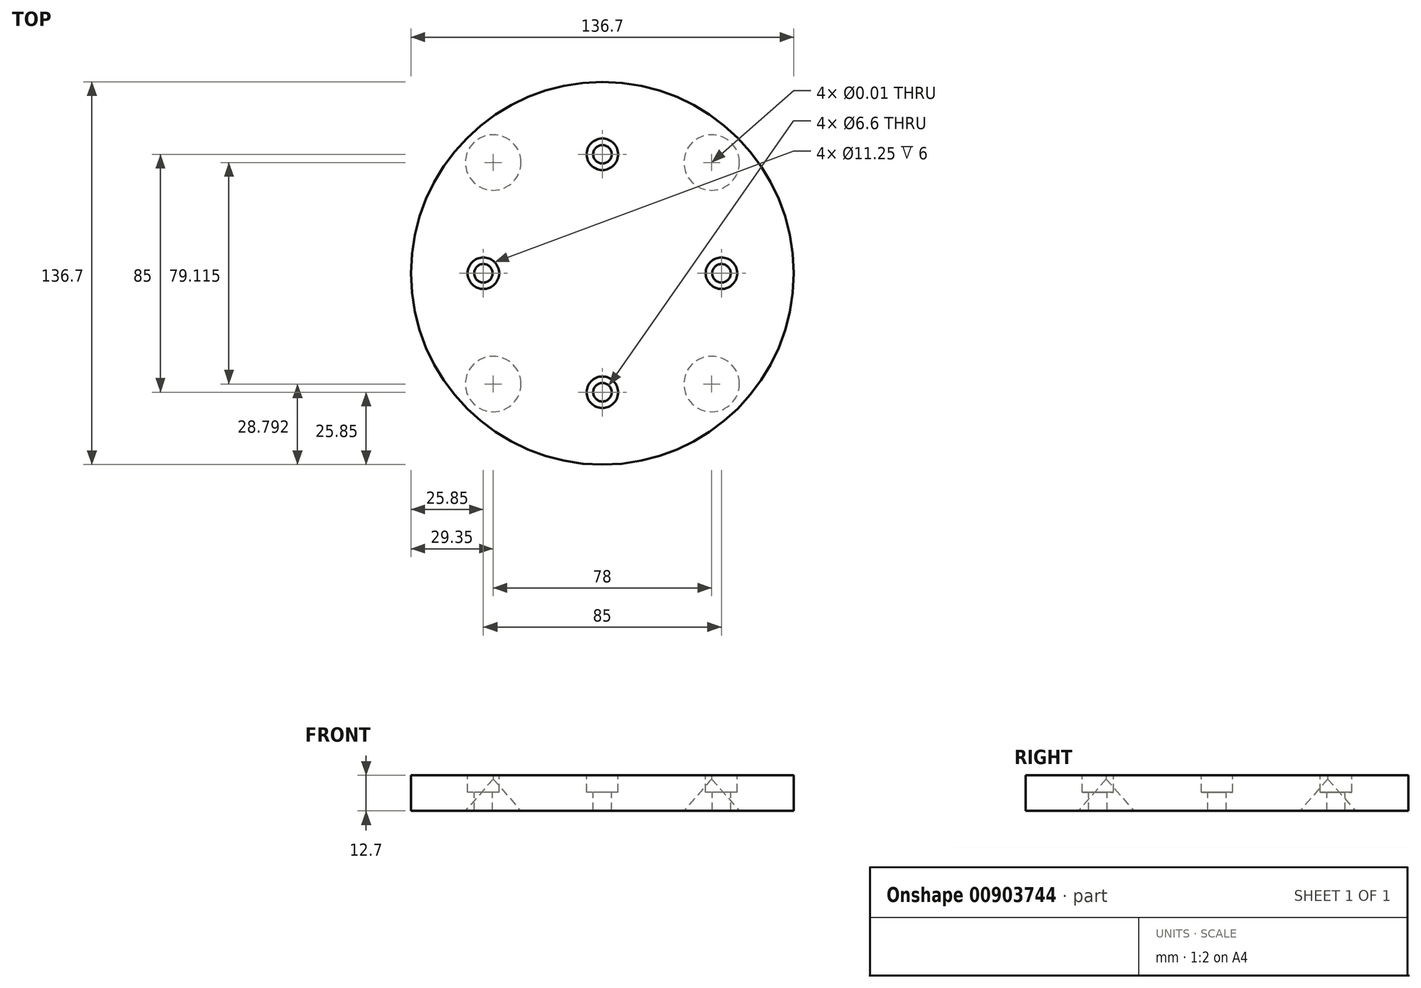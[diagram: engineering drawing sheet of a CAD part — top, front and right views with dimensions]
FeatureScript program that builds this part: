
annotation { "Feature Type Name" : "Feature", "Feature Type Description" : "" }
export const myFeature = defineFeature(function(context is Context, id is Id, definition is map)
    precondition{}
    {
        {
            var Q0;
            Q0=qCreatedBy(makeId("Top.planeOp"),FACE);
            cPlane(context, id + "F0", {"entities" : qUnion([Q0]), "cplaneType" : CPlaneType.OFFSET, "offset" : 12.7 * mm, "width" : 152.4 * mm, "height" : 152.4 * mm});
        }
        {
            var Q0;
            Q0=qCreatedBy(makeId("Top.planeOp"),FACE);
            var sketch = newSketch(context, id + "F1", { "sketchPlane" : qUnion([Q0])});
            skCircle(sketch, "E0", {"center": v(0, 0) * mm, "radius": 68.35 * mm});
            skSolve(sketch);
        }
        {
            var Q0;
            Q0 = qSketchRegion(id + "F1", true);
            extrude(context, id + "F2", {"entities" : qUnion([Q0]), "depth" : 12.7 * mm, "offsetDistance" : 25.4 * mm});
        }
        {
            var Q0;
            Q0=qCreatedBy(makeId("Top.planeOp"),FACE);
            var sketch = newSketch(context, id + "F3", { "sketchPlane" : qUnion([Q0])});
            skPoint(sketch, "E1", {"position": v(39, 39.56) * mm});
            skPoint(sketch, "E2", {"position": v(-39, 39.56) * mm});
            skPoint(sketch, "E3", {"position": v(-39, -39.56) * mm});
            skCircle(sketch, "E4", {"center": v(0, 0) * mm, "radius": 55.55 * mm});
            skPoint(sketch, "E5.MirrorP", {"position": v(39, -39.56) * mm});
            skSolve(sketch);
        }
        {
            var Q0;
            Q0=sQuery(id+"F3.wireOp",VERTEX,"E2");
            var Q1;
            Q1=sQuery(id+"F3.wireOp",VERTEX,"E1");
            var Q2;
            Q2=sQuery(id+"F3.wireOp",VERTEX,"f3bf48b2-0e91-47d8-8b82-7dac251cd858");
            var Q3;
            Q3=sQuery(id+"F3.wireOp",VERTEX,"E3");
            var Q4;
            Q4=sQuery(id+"F3.wireOp",VERTEX,"E5.MirrorP");
            var Q5;
            Q5=makeQuery(id+"F2.opExtrude","SWEPT_BODY",BODY,{"disambiguationData":[OSD([sQuery(id+"F1.wireOp",EDGE,"E0")])]});
            hole(context, id + "F4", {"style" : HoleStyle.C_SINK, "endStyle" : HoleEndStyle.THROUGH, "oppositeDirection" : true, "standardTappedOrClearance" : lookupTablePath({ "standard" : "ANSI", "size" : "3/8 (0.38)", "type" : "Drilled" }), "standardBlindInLast" : lookupTablePath({ "standard" : "ANSI", "size" : "3/8", "type" : "Drilled" }), "holeDiameter" : 3 / 203.2 * mm, "cSinkDiameter" : 19.84 * mm, "cSinkAngle" : 82 * degree, "majorDiameter" : 6.35 * mm, "isTappedThrough" : true, "tappedDepth" : 12.7 * mm, "tapClearance" : 3, "startFromSketch" : true, "locations" : qUnion([Q0, Q1, Q2, Q3, Q4]), "scope" : qUnion([Q5])});
        }
        {
            var Q0;
            Q0=qCreatedBy(id+"F0.planeOp",FACE);
            var sketch = newSketch(context, id + "F5", { "sketchPlane" : qUnion([Q0])});
            skPoint(sketch, "E6", {"position": v(0, 42.5) * mm});
            skPoint(sketch, "E7", {"position": v(42.5, 0) * mm});
            skPoint(sketch, "E8", {"position": v(-42.5, 0) * mm});
            skPoint(sketch, "E9", {"position": v(0, -42.5) * mm});
            skSolve(sketch);
        }
        {
            var Q0;
            Q0=sQuery(id+"F5.wireOp",VERTEX,"E6");
            var Q1;
            Q1=sQuery(id+"F5.wireOp",VERTEX,"E7");
            var Q2;
            Q2=sQuery(id+"F5.wireOp",VERTEX,"E9");
            var Q3;
            Q3=sQuery(id+"F5.wireOp",VERTEX,"E8");
            var Q4;
            Q4=makeQuery(id+"F2.opExtrude","SWEPT_BODY",BODY,{"disambiguationData":[OSD([sQuery(id+"F1.wireOp",EDGE,"E0")])]});
            hole(context, id + "F6", {"style" : HoleStyle.C_BORE, "endStyle" : HoleEndStyle.THROUGH, "standardTappedOrClearance" : lookupTablePath({ "fit" : "Normal", "standard" : "ISO", "size" : "M6", "type" : "Clearance" }), "standardBlindInLast" : lookupTablePath({ "fit" : "Normal", "standard" : "ISO", "size" : "M6", "type" : "Clearance" }), "holeDiameter" : 6.6 * mm, "cBoreDiameter" : 11.25 * mm, "cBoreDepth" : 6 * mm, "majorDiameter" : 6.35 * mm, "isTappedThrough" : true, "tappedDepth" : 12.7 * mm, "tapClearance" : 3, "startFromSketch" : true, "locations" : qUnion([Q0, Q1, Q2, Q3]), "scope" : qUnion([Q4])});
        }
    });
